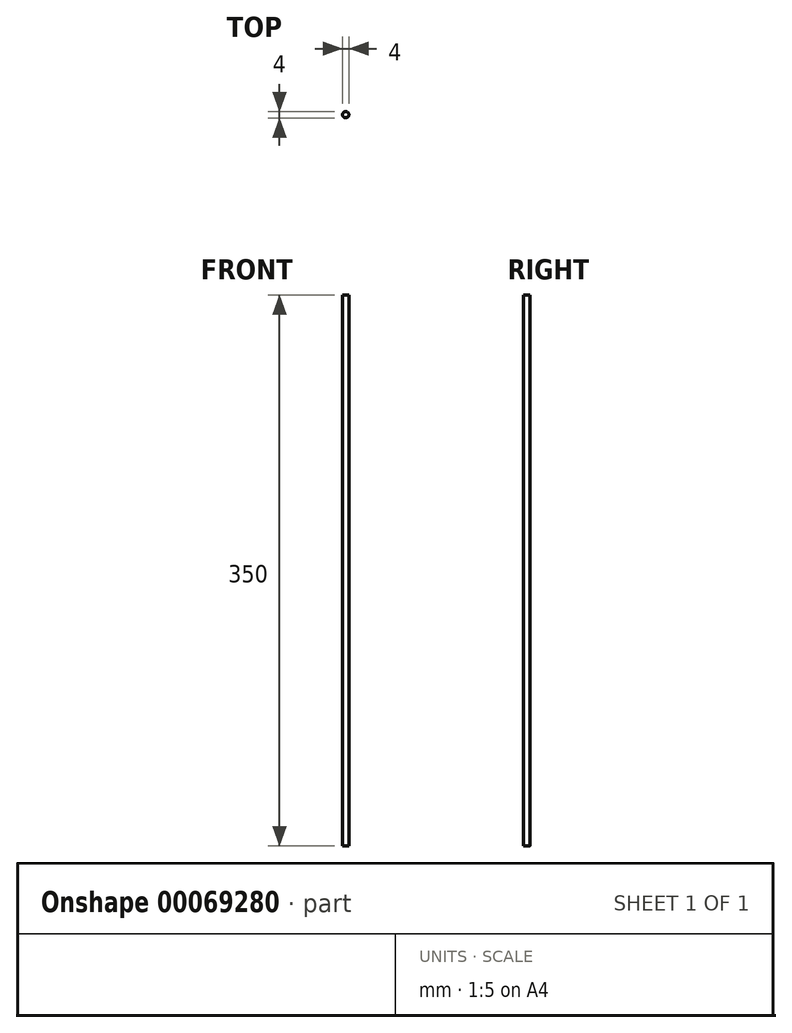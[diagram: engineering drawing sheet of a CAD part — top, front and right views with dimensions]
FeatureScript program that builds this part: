
annotation { "Feature Type Name" : "Feature", "Feature Type Description" : "" }
export const myFeature = defineFeature(function(context is Context, id is Id, definition is map)
    precondition{}
    {
        {
            var Q0;
            Q0=qCreatedBy(makeId("Top.planeOp"),FACE);
            var sketch = newSketch(context, id + "F0", { "sketchPlane" : qUnion([Q0])});
            skCircle(sketch, "E0", {"center": v(0, 0) * mm, "radius": 2 * mm});
            skSolve(sketch);
        }
        {
            var Q0;
            Q0 = qSketchRegion(id + "F0", true);
            extrude(context, id + "F1", {"entities" : qUnion([Q0]), "depth" : 350 * mm});
        }
    });
